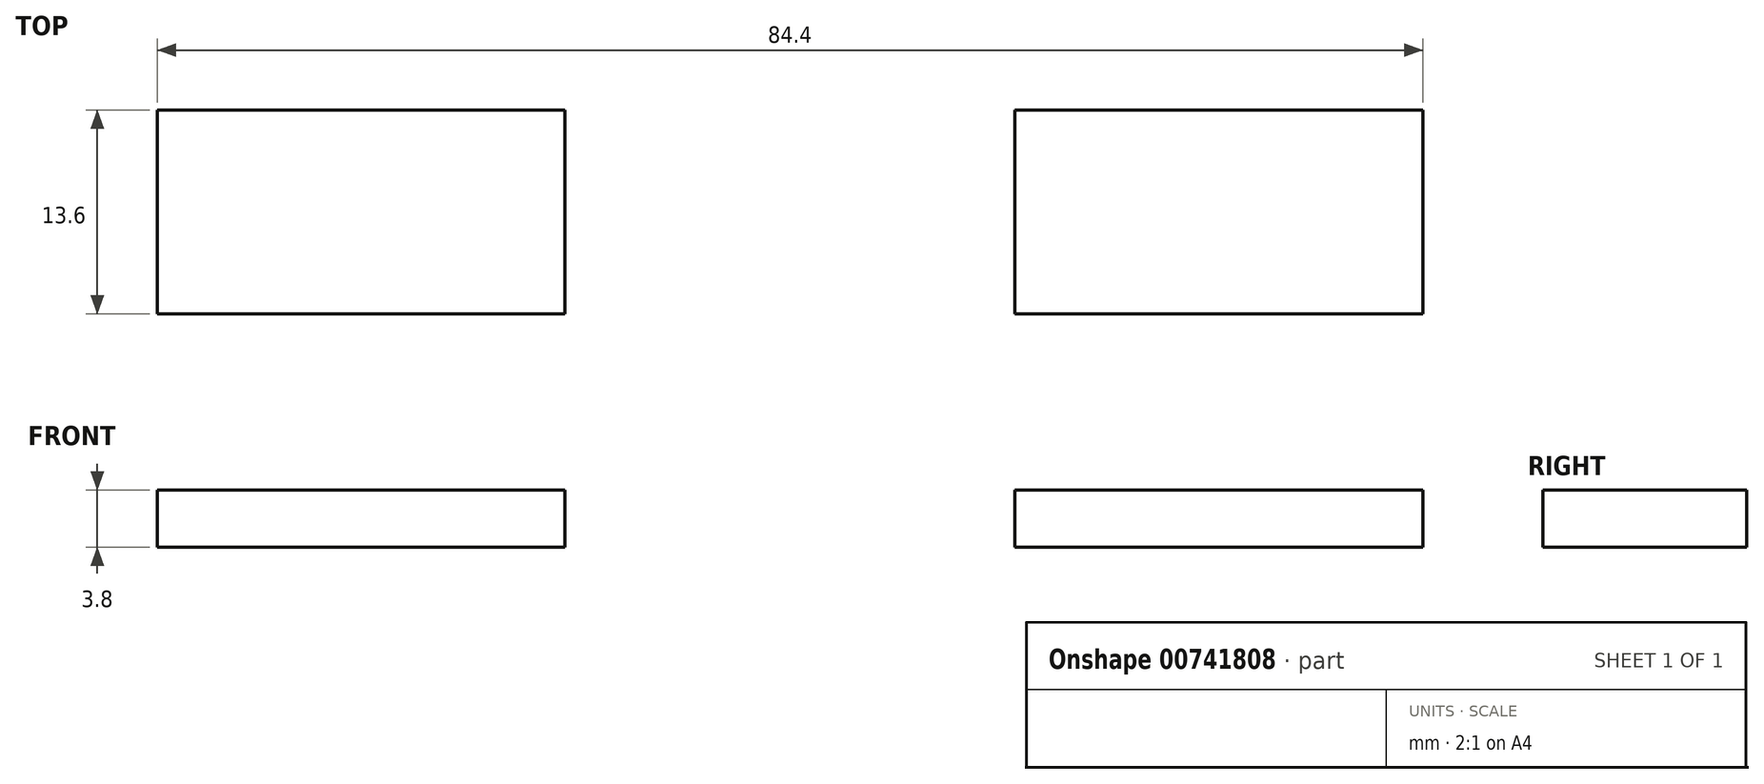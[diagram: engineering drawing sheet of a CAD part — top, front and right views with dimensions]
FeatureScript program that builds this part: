
annotation { "Feature Type Name" : "Feature", "Feature Type Description" : "" }
export const myFeature = defineFeature(function(context is Context, id is Id, definition is map)
    precondition{}
    {
        {
            var Q0;
            Q0=qCreatedBy(makeId("Top.planeOp"),FACE);
            var sketch = newSketch(context, id + "F0", { "sketchPlane" : qUnion([Q0])});
            skLineSegment(sketch, "E0.bottom", {"start": v(-220.8, 51.3) * mm, "end": v(229.2, 51.3) * mm});
            skLineSegment(sketch, "E0.top", {"start": v(-220.8, -98.7) * mm, "end": v(229.2, -98.7) * mm});
            skLineSegment(sketch, "E0.left", {"start": v(-220.8, 51.3) * mm, "end": v(-220.8, -98.7) * mm});
            skLineSegment(sketch, "E0.right", {"start": v(229.2, 51.3) * mm, "end": v(229.2, -98.7) * mm});
            skLineSegment(sketch, "E1", {"start": v(-152.8, -98.7) * mm, "end": v(-152.8, -85.1) * mm});
            skLineSegment(sketch, "E2", {"start": v(-152.8, -85.1) * mm, "end": v(-125.6, -85.1) * mm});
            skLineSegment(sketch, "E3", {"start": v(-125.6, -85.1) * mm, "end": v(-125.6, -98.7) * mm});
            skLineSegment(sketch, "E4", {"start": v(-125.6, -98.7) * mm, "end": v(-95.6, -98.7) * mm});
            skLineSegment(sketch, "E5", {"start": v(-95.6, -98.7) * mm, "end": v(-95.6, -85.1) * mm});
            skLineSegment(sketch, "E6", {"start": v(-95.6, -85.1) * mm, "end": v(-68.4, -85.1) * mm});
            skLineSegment(sketch, "E7", {"start": v(-68.4, -85.1) * mm, "end": v(-68.4, -98.7) * mm});
            skSolve(sketch);
        }
        {
            var Q0;
            {var subQ0=sQuery(id+"F0.wireOp",EDGE,"E1");Q0=makeQuery(id+"F0.imprint","IMPRINT",FACE,{"disambiguationData":[TD([[makeQuery(id+"F0.imprint","IMPRINT",EDGE,{"derivedFrom":subQ0}),-1.0]])]});}
            var Q1;
            {var subQ0=sQuery(id+"F0.wireOp",EDGE,"E5");Q1=makeQuery(id+"F0.imprint","IMPRINT",FACE,{"disambiguationData":[TD([[makeQuery(id+"F0.imprint","IMPRINT",EDGE,{"derivedFrom":subQ0}),-1.0]])]});}
            extrude(context, id + "F1", {"entities" : qUnion([Q0, Q1]), "depth" : 3.8 * mm, "offsetDistance" : 25 * mm});
        }
    });
